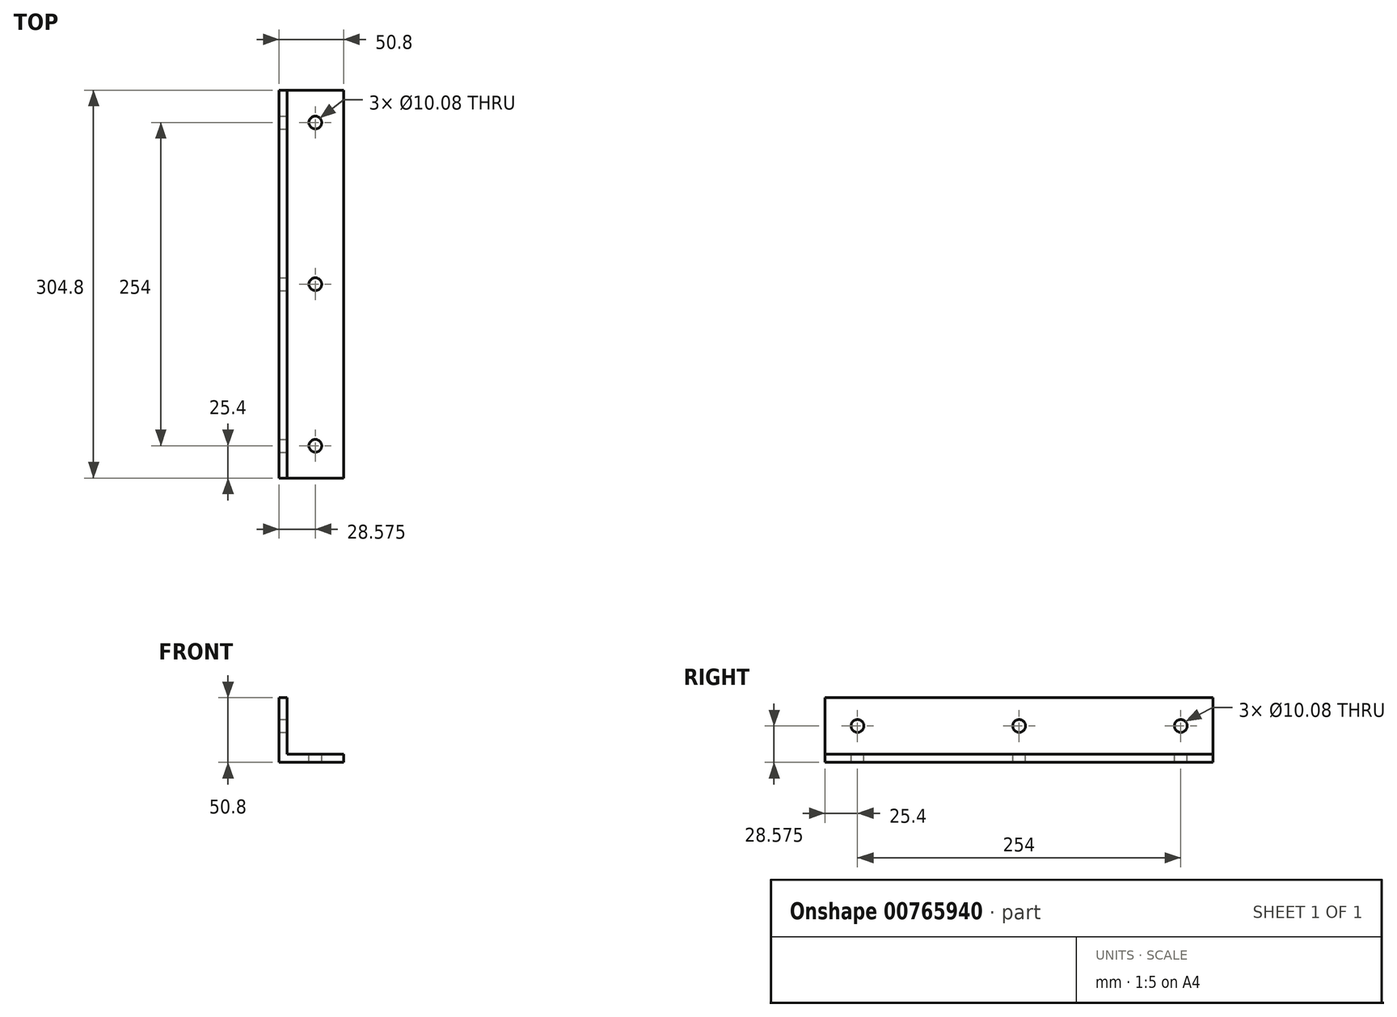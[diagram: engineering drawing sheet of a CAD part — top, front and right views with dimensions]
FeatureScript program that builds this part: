
annotation { "Feature Type Name" : "Feature", "Feature Type Description" : "" }
export const myFeature = defineFeature(function(context is Context, id is Id, definition is map)
    precondition{}
    {
        {
            var Q0;
            Q0=qCreatedBy(makeId("Front.planeOp"),FACE);
            var sketch = newSketch(context, id + "F0", { "sketchPlane" : qUnion([Q0])});
            skLineSegment(sketch, "E0", {"start": v(0, 0) * mm, "end": v(0, 50.8) * mm});
            skLineSegment(sketch, "E1", {"start": v(0, 50.8) * mm, "end": v(6.35, 50.8) * mm});
            skLineSegment(sketch, "E2", {"start": v(6.35, 50.8) * mm, "end": v(6.35, 6.35) * mm});
            skLineSegment(sketch, "E3", {"start": v(6.35, 6.35) * mm, "end": v(50.8, 6.35) * mm});
            skLineSegment(sketch, "E4", {"start": v(50.8, 6.35) * mm, "end": v(50.8, 0) * mm});
            skLineSegment(sketch, "E5", {"start": v(50.8, 0) * mm, "end": v(0, 0) * mm});
            skSolve(sketch);
        }
        {
            var Q0;
            Q0 = qSketchRegion(id + "F0", true);
            extrude(context, id + "F1", {"entities" : qUnion([Q0]), "depth" : 304.8 * mm, "offsetDistance" : 25.4 * mm});
        }
        {
            var Q0;
            Q0=makeQuery(id+"F1.opExtrude","SWEPT_FACE",FACE,{"disambiguationData":[OSD([sQuery(id+"F0.wireOp",EDGE,"E2")])]});
            var sketch = newSketch(context, id + "F2", { "sketchPlane" : qUnion([Q0])});
            skLineSegment(sketch, "E6", {"start": v(-304.8, 28.57) * mm, "end": v(0, 28.57) * mm, "construction": true});
            skPoint(sketch, "E7", {"position": v(-279.4, 28.57) * mm});
            skPoint(sketch, "E8", {"position": v(-25.4, 28.58) * mm});
            skPoint(sketch, "E9", {"position": v(-152.4, 28.57) * mm});
            skSolve(sketch);
        }
        {
            var Q0;
            Q0=makeQuery(id+"F1.opExtrude","SWEPT_FACE",FACE,{"disambiguationData":[OSD([sQuery(id+"F0.wireOp",EDGE,"E3")])]});
            var sketch = newSketch(context, id + "F3", { "sketchPlane" : qUnion([Q0])});
            skLineSegment(sketch, "E10", {"start": v(28.58, 0) * mm, "end": v(28.58, -304.8) * mm, "construction": true});
            skPoint(sketch, "E11", {"position": v(28.58, -279.4) * mm});
            skPoint(sketch, "E12", {"position": v(28.58, -152.4) * mm});
            skPoint(sketch, "E13", {"position": v(28.58, -25.4) * mm});
            skSolve(sketch);
        }
        {
            var Q0;
            Q0=sQuery(id+"F3.wireOp",VERTEX,"E12");
            var Q1;
            Q1=sQuery(id+"F3.wireOp",VERTEX,"E13");
            var Q2;
            Q2=sQuery(id+"F3.wireOp",VERTEX,"E11");
            var Q3;
            Q3=sQuery(id+"F2.wireOp",VERTEX,"E7");
            var Q4;
            Q4=sQuery(id+"F2.wireOp",VERTEX,"E9");
            var Q5;
            Q5=sQuery(id+"F2.wireOp",VERTEX,"E8");
            var Q6;
            Q6=makeQuery(id+"F1.opExtrude","SWEPT_BODY",BODY,{"disambiguationData":[OSD([sQuery(id+"F0.wireOp",EDGE,"E0"),sQuery(id+"F0.wireOp",EDGE,"E1"),sQuery(id+"F0.wireOp",EDGE,"E2"),sQuery(id+"F0.wireOp",EDGE,"E3"),sQuery(id+"F0.wireOp",EDGE,"E4"),sQuery(id+"F0.wireOp",EDGE,"E5")])]});
            hole(context, id + "F4", {"style" : HoleStyle.SIMPLE, "endStyle" : HoleEndStyle.BLIND, "standardTappedOrClearance" : lookupTablePath({ "standard" : "ANSI", "fit" : "Normal (ASME)", "size" : "3/8", "type" : "Clearance" }), "standardBlindInLast" : lookupTablePath({ "fit" : "Free", "standard" : "ANSI", "size" : "3/8", "type" : "Clearance" }), "holeDiameter" : 10.08 * mm, "majorDiameter" : 6.35 * mm, "holeDepth" : 20.65 * mm, "isTappedThrough" : true, "tappedDepth" : 15.9 * mm, "tapClearance" : 3, "locations" : qUnion([Q0, Q1, Q2, Q3, Q4, Q5]), "scope" : qUnion([Q6])});
        }
    });
